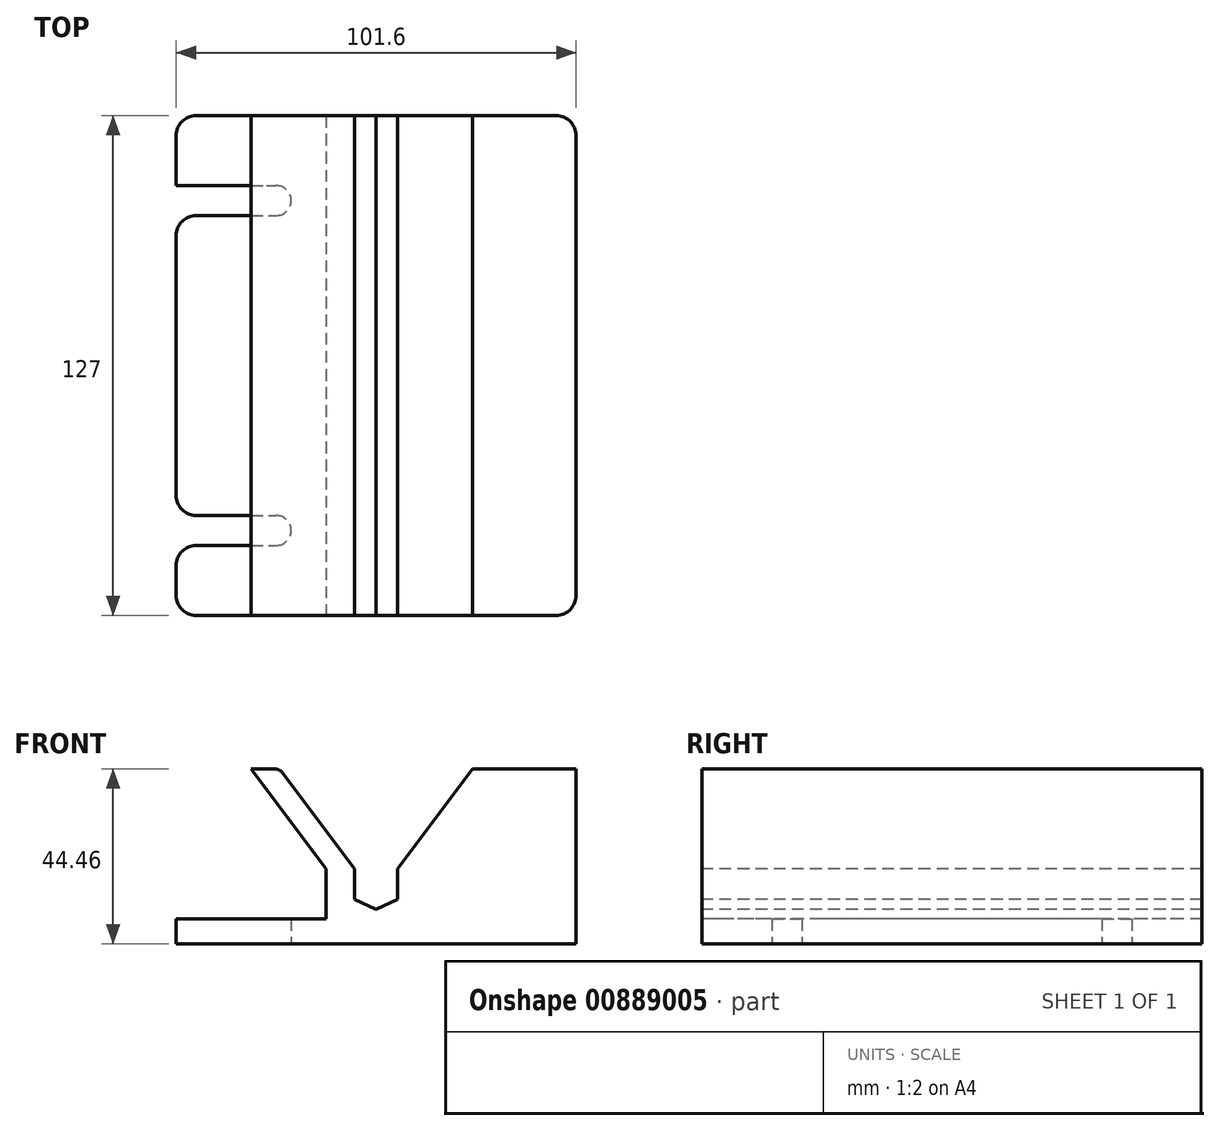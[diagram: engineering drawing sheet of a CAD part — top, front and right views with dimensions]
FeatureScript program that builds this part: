
annotation { "Feature Type Name" : "Feature", "Feature Type Description" : "" }
export const myFeature = defineFeature(function(context is Context, id is Id, definition is map)
    precondition{}
    {
        {
            var Q0;
            Q0=qCreatedBy(makeId("Front.planeOp"),FACE);
            var sketch = newSketch(context, id + "F0", { "sketchPlane" : qUnion([Q0])});
            skLineSegment(sketch, "E0.bottom", {"start": v(50.8, -22.23) * mm, "end": v(-50.8, -22.23) * mm});
            skLineSegment(sketch, "E0.top", {"start": v(50.8, 22.23) * mm, "end": v(-50.8, 22.23) * mm});
            skLineSegment(sketch, "E0.left", {"start": v(50.8, -22.23) * mm, "end": v(50.8, 22.23) * mm});
            skLineSegment(sketch, "E0.right", {"start": v(-50.8, -22.23) * mm, "end": v(-50.8, 22.22) * mm});
            skPoint(sketch, "E0.middle", {"position": v(0, 0) * mm});
            skSolve(sketch);
        }
        {
            var Q0;
            Q0=makeQuery(id+"F0.imprint","IMPRINT",FACE,{"disambiguationData":[TD([[makeQuery(id+"F0.imprint","IMPRINT",EDGE,{"derivedFrom":sQuery(id+"F0.wireOp",EDGE,"E0.bottom")}),-1.0]])]});
            extrude(context, id + "F1", {"entities" : qUnion([Q0]), "endBound" : BoundingType.SYMMETRIC, "depth" : 127 * mm, "offsetDistance" : 25.4 * mm});
        }
        {
            var Q0;
            Q0=makeQuery(id+"F1.opExtrude","CAP_FACE",FACE,{"disambiguationData":[OSD([sQuery(id+"F0.wireOp",EDGE,"E0.bottom"),sQuery(id+"F0.wireOp",EDGE,"E0.top"),sQuery(id+"F0.wireOp",EDGE,"E0.left"),sQuery(id+"F0.wireOp",EDGE,"E0.right")])],"isStart":false});
            var sketch = newSketch(context, id + "F2", { "sketchPlane" : qUnion([Q0])});
            skLineSegment(sketch, "E1", {"start": v(-12.7, -15.88) * mm, "end": v(-50.8, -15.88) * mm});
            skLineSegment(sketch, "E2", {"start": v(-50.8, -15.88) * mm, "end": v(-50.8, 22.22) * mm});
            skLineSegment(sketch, "E3", {"start": v(-50.8, 22.22) * mm, "end": v(-31.75, 22.23) * mm});
            skLineSegment(sketch, "E4", {"start": v(-31.75, 22.23) * mm, "end": v(-12.7, -3.18) * mm});
            skLineSegment(sketch, "E5", {"start": v(-12.7, -3.18) * mm, "end": v(-12.7, -15.88) * mm});
            skSolve(sketch);
        }
        {
            var Q0;
            Q0=makeQuery(id+"F2.imprint","IMPRINT",FACE,{"disambiguationData":[TD([[makeQuery(id+"F2.imprint","IMPRINT",EDGE,{"derivedFrom":sQuery(id+"F2.wireOp",EDGE,"E1")}),-1.0]])]});
            extrude(context, id + "F3", {"entities" : qUnion([Q0]), "operationType" : NewBodyOperationType.REMOVE, "endBound" : BoundingType.THROUGH_ALL, "oppositeDirection" : true, "depth" : 25.4 * mm, "offsetDistance" : 25.4 * mm});
        }
        {
            var Q0;
            Q0=makeQuery(id+"F1.opExtrude","CAP_FACE",FACE,{"disambiguationData":[OSD([sQuery(id+"F0.wireOp",EDGE,"E0.bottom"),sQuery(id+"F0.wireOp",EDGE,"E0.top"),sQuery(id+"F0.wireOp",EDGE,"E0.left"),sQuery(id+"F0.wireOp",EDGE,"E0.right")])],"isStart":false});
            var sketch = newSketch(context, id + "F4", { "sketchPlane" : qUnion([Q0])});
            skLineSegment(sketch, "E6", {"start": v(-24.51, 22.22) * mm, "end": v(-5.46, -3.18) * mm});
            skLineSegment(sketch, "E7", {"start": v(-5.46, -3.18) * mm, "end": v(-5.46, -10.9) * mm});
            skLineSegment(sketch, "E8", {"start": v(-5.46, -10.9) * mm, "end": v(0, -13.45) * mm});
            skLineSegment(sketch, "E9", {"start": v(0, -13.45) * mm, "end": v(5.46, -10.9) * mm});
            skLineSegment(sketch, "E10", {"start": v(5.46, -10.9) * mm, "end": v(5.46, -3.18) * mm});
            skLineSegment(sketch, "E11", {"start": v(5.46, -3.18) * mm, "end": v(24.51, 22.23) * mm});
            skLineSegment(sketch, "E12", {"start": v(24.51, 22.23) * mm, "end": v(-24.51, 22.23) * mm});
            skSolve(sketch);
        }
        {
            var Q0;
            Q0=makeQuery(id+"F4.imprint","IMPRINT",FACE,{"disambiguationData":[TD([[makeQuery(id+"F4.imprint","IMPRINT",EDGE,{"derivedFrom":sQuery(id+"F4.wireOp",EDGE,"E6")}),1.0]])]});
            extrude(context, id + "F5", {"entities" : qUnion([Q0]), "operationType" : NewBodyOperationType.REMOVE, "endBound" : BoundingType.THROUGH_ALL, "oppositeDirection" : true, "depth" : 25.4 * mm, "offsetDistance" : 25.4 * mm});
        }
        {
            var Q0;
            Q0=makeQuery(id+"F3.boolean.opBoolean","COPY",EDGE,{"derivedFrom":makeQuery(id+"F3.opExtrude","SWEPT_EDGE",EDGE,{"disambiguationData":[OSD([sQuery(id+"F0.wireOp",EDGE,"E0.top"),sQuery(id+"F2.wireOp",EDGE,"E3"),sQuery(id+"F2.wireOp",EDGE,"E4")])]})});
            var Q1;
            Q1=makeQuery(id+"F5.boolean.opBoolean","COPY",EDGE,{"derivedFrom":makeQuery(id+"F5.opExtrude","SWEPT_EDGE",EDGE,{"disambiguationData":[OSD([sQuery(id+"F0.wireOp",EDGE,"E0.top"),sQuery(id+"F4.wireOp",EDGE,"E6"),sQuery(id+"F4.wireOp",EDGE,"E12")])]})});
            var Q2;
            Q2=makeQuery(id+"F5.boolean.opBoolean","COPY",EDGE,{"derivedFrom":makeQuery(id+"F5.opExtrude","SWEPT_EDGE",EDGE,{"disambiguationData":[OSD([sQuery(id+"F0.wireOp",EDGE,"E0.top"),sQuery(id+"F4.wireOp",EDGE,"E11"),sQuery(id+"F4.wireOp",EDGE,"E12")])]})});
            var Q3;
            Q3=makeQuery(id+"FReAnOjBeKejbQ6_1.1.F3.boolean.opBoolean","COPY",EDGE,{"derivedFrom":makeQuery(id+"FReAnOjBeKejbQ6_1.1.F3.opExtrude","SWEPT_EDGE",EDGE,{"disambiguationData":[OSD([sQuery(id+"F0.wireOp",EDGE,"E0.top"),sQuery(id+"F2.wireOp",EDGE,"E3"),sQuery(id+"F2.wireOp",EDGE,"E4")])]})});
            fillet(context, id + "F6", {"entities" : qUnion([Q0, Q1, Q2, Q3]), "radius" : 2.54 * mm, "tangentPropagation" : true, "allowEdgeOverflow" : false});
        }
        {
            var Q0;
            Q0=makeQuery(id+"F1.opExtrude","SWEPT_FACE",FACE,{"disambiguationData":[OSD([sQuery(id+"F0.wireOp",EDGE,"E0.bottom")])]});
            var sketch = newSketch(context, id + "F7", { "sketchPlane" : qUnion([Q0])});
            skLineSegment(sketch, "E13.bottom", {"start": v(-50.8, 45.72) * mm, "end": v(-25.4, 45.72) * mm});
            skLineSegment(sketch, "E13.top", {"start": v(-50.8, 38.1) * mm, "end": v(-25.4, 38.1) * mm});
            skLineSegment(sketch, "E13.left", {"start": v(-50.8, 45.72) * mm, "end": v(-50.8, 38.1) * mm});
            skLineSegment(sketch, "E13.right", {"start": v(-25.4, 45.72) * mm, "end": v(-25.4, 38.1) * mm, "construction": true});
            skLineSegment(sketch, "E14.bottom", {"start": v(-50.8, -38.1) * mm, "end": v(-25.4, -38.1) * mm});
            skLineSegment(sketch, "E14.top", {"start": v(-50.8, -45.72) * mm, "end": v(-25.4, -45.72) * mm});
            skLineSegment(sketch, "E14.left", {"start": v(-50.8, -38.1) * mm, "end": v(-50.8, -45.72) * mm});
            skLineSegment(sketch, "E14.right", {"start": v(-25.4, -38.1) * mm, "end": v(-25.4, -45.72) * mm, "construction": true});
            skArc(sketch, "E15", {"start": v(-25.4, 38.1) * mm, "mid": v(-21.59, 41.91) * mm, "end": v(-25.4, 45.72) * mm});
            skArc(sketch, "E16", {"start": v(-25.4, -45.72) * mm, "mid": v(-21.59, -41.9) * mm, "end": v(-25.4, -38.1) * mm});
            skSolve(sketch);
        }
        {
            var Q0;
            Q0 = qSketchRegion(id + "F7", true);
            var Q1;
            Q1=makeQuery(id+"F3.boolean.opBoolean","COPY",FACE,{"derivedFrom":makeQuery(id+"F3.opExtrude","SWEPT_FACE",FACE,{"disambiguationData":[OSD([sQuery(id+"F2.wireOp",EDGE,"E1")])]})});
            extrude(context, id + "F8", {"entities" : qUnion([Q0]), "operationType" : NewBodyOperationType.REMOVE, "endBound" : BoundingType.UP_TO_SURFACE, "oppositeDirection" : true, "depth" : 25.4 * mm, "endBoundEntityFace" : qUnion([Q1]), "offsetDistance" : 25.4 * mm});
        }
        {
            var Q0;
            Q0=makeQuery(id+"F1.opExtrude","CAP_EDGE",EDGE,{"disambiguationData":[OSD([sQuery(id+"F0.wireOp",EDGE,"E0.right")])],"isStart":false});
            var Q1;
            Q1=makeQuery(id+"F1.opExtrude","CAP_EDGE",EDGE,{"disambiguationData":[OSD([sQuery(id+"F0.wireOp",EDGE,"E0.right")])],"isStart":true});
            var Q2;
            Q2=makeQuery(id+"F1.opExtrude","CAP_EDGE",EDGE,{"disambiguationData":[OSD([sQuery(id+"F0.wireOp",EDGE,"E0.left")])],"isStart":false});
            var Q3;
            Q3=makeQuery(id+"F1.opExtrude","CAP_EDGE",EDGE,{"disambiguationData":[OSD([sQuery(id+"F0.wireOp",EDGE,"E0.left")])],"isStart":true});
            var Q4;
            Q4=makeQuery(id+"F2x58J9mWKbWmGX_1.1.F8.boolean.opBoolean","COPY",EDGE,{"derivedFrom":makeQuery(id+"F2x58J9mWKbWmGX_1.1.F8.opExtrude","SWEPT_EDGE",EDGE,{"disambiguationData":[OSD([sQuery(id+"F0.wireOp",EDGE,"E0.bottom"),sQuery(id+"F0.wireOp",EDGE,"E0.right"),sQuery(id+"F7.wireOp",EDGE,"E13.bottom"),sQuery(id+"F7.wireOp",EDGE,"E13.left")])]})});
            var Q5;
            Q5=makeQuery(id+"F2x58J9mWKbWmGX_1.1.F8.boolean.opBoolean","COPY",EDGE,{"derivedFrom":makeQuery(id+"F2x58J9mWKbWmGX_1.1.F8.opExtrude","SWEPT_EDGE",EDGE,{"disambiguationData":[OSD([sQuery(id+"F0.wireOp",EDGE,"E0.bottom"),sQuery(id+"F0.wireOp",EDGE,"E0.right"),sQuery(id+"F7.wireOp",EDGE,"E13.top"),sQuery(id+"F7.wireOp",EDGE,"E13.left")])]})});
            var Q6;
            Q6=makeQuery(id+"F2x58J9mWKbWmGX_1.1.F8.boolean.opBoolean","COPY",EDGE,{"derivedFrom":makeQuery(id+"F2x58J9mWKbWmGX_1.1.F8.opExtrude","SWEPT_EDGE",EDGE,{"disambiguationData":[OSD([sQuery(id+"F0.wireOp",EDGE,"E0.bottom"),sQuery(id+"F0.wireOp",EDGE,"E0.right"),sQuery(id+"F7.wireOp",EDGE,"E14.bottom"),sQuery(id+"F7.wireOp",EDGE,"E14.left")])]})});
            var Q7;
            Q7=makeQuery(id+"F2x58J9mWKbWmGX_1.1.F8.boolean.opBoolean","COPY",EDGE,{"derivedFrom":makeQuery(id+"F2x58J9mWKbWmGX_1.1.F8.opExtrude","SWEPT_EDGE",EDGE,{"disambiguationData":[OSD([sQuery(id+"F0.wireOp",EDGE,"E0.bottom"),sQuery(id+"F0.wireOp",EDGE,"E0.right"),sQuery(id+"F7.wireOp",EDGE,"E14.top"),sQuery(id+"F7.wireOp",EDGE,"E14.left")])]})});
            var Q8;
            Q8=makeQuery(id+"F8.boolean.opBoolean","COPY",EDGE,{"derivedFrom":makeQuery(id+"F8.opExtrude","SWEPT_EDGE",EDGE,{"disambiguationData":[OSD([sQuery(id+"F0.wireOp",EDGE,"E0.bottom"),sQuery(id+"F0.wireOp",EDGE,"E0.right"),sQuery(id+"F7.wireOp",EDGE,"E13.bottom"),sQuery(id+"F7.wireOp",EDGE,"E13.left")])]})});
            var Q9;
            Q9=makeQuery(id+"F8.boolean.opBoolean","COPY",EDGE,{"derivedFrom":makeQuery(id+"F8.opExtrude","SWEPT_EDGE",EDGE,{"disambiguationData":[OSD([sQuery(id+"F0.wireOp",EDGE,"E0.bottom"),sQuery(id+"F0.wireOp",EDGE,"E0.right"),sQuery(id+"F7.wireOp",EDGE,"E14.bottom"),sQuery(id+"F7.wireOp",EDGE,"E14.left")])]})});
            var Q10;
            Q10=makeQuery(id+"F8.boolean.opBoolean","COPY",EDGE,{"derivedFrom":makeQuery(id+"F8.opExtrude","SWEPT_EDGE",EDGE,{"disambiguationData":[OSD([sQuery(id+"F0.wireOp",EDGE,"E0.bottom"),sQuery(id+"F0.wireOp",EDGE,"E0.right"),sQuery(id+"F7.wireOp",EDGE,"E14.top"),sQuery(id+"F7.wireOp",EDGE,"E14.left")])]})});
            var Q11;
            Q11=makeQuery(id+"F8.boolean.opBoolean","COPY",EDGE,{"derivedFrom":makeQuery(id+"F8.opExtrude","SWEPT_EDGE",EDGE,{"disambiguationData":[OSD([sQuery(id+"F0.wireOp",EDGE,"E0.bottom"),sQuery(id+"F0.wireOp",EDGE,"E0.right"),sQuery(id+"F7.wireOp",EDGE,"E13.top"),sQuery(id+"F7.wireOp",EDGE,"E13.left")])]})});
            fillet(context, id + "F9", {"entities" : qUnion([Q0, Q1, Q2, Q3, Q4, Q5, Q6, Q7, Q8, Q9, Q10, Q11]), "radius" : 5.08 * mm, "tangentPropagation" : true, "allowEdgeOverflow" : false});
        }
    });
